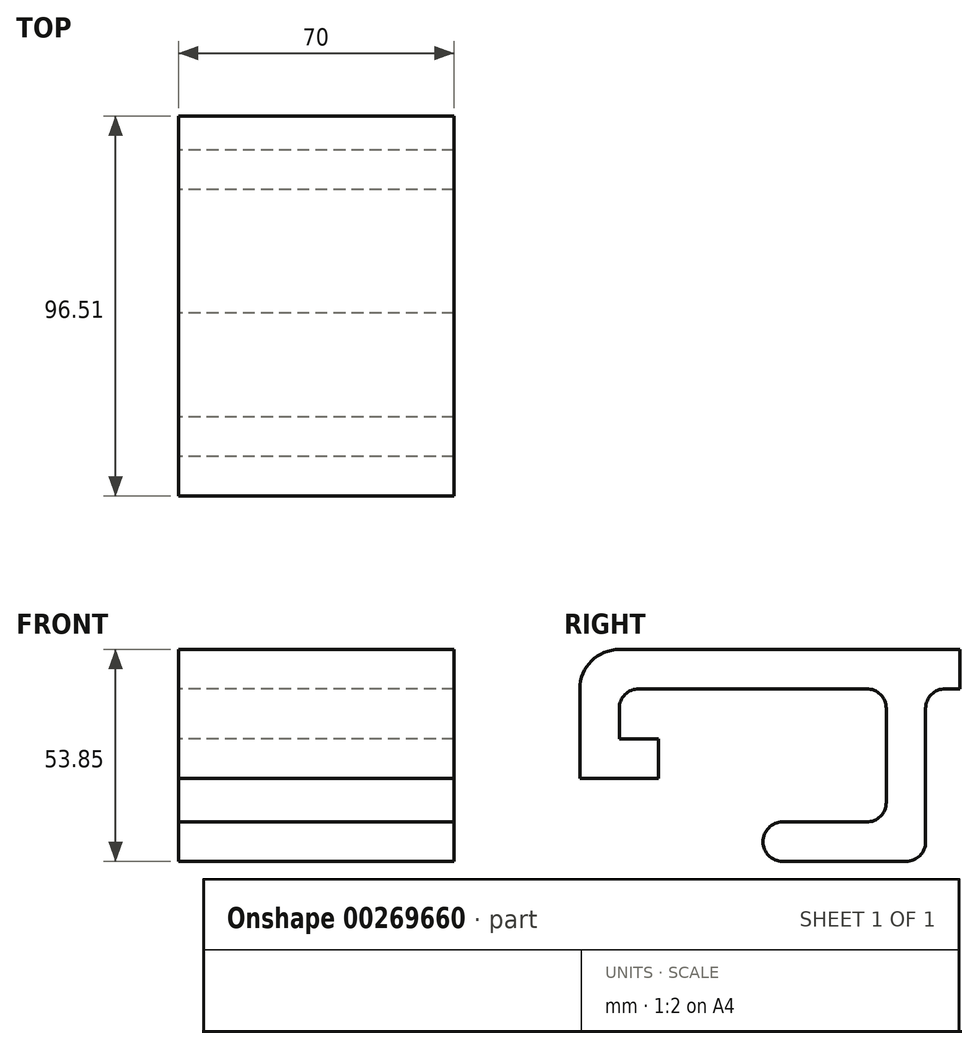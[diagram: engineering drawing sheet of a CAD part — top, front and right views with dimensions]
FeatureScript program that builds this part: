
annotation { "Feature Type Name" : "Feature", "Feature Type Description" : "" }
export const myFeature = defineFeature(function(context is Context, id is Id, definition is map)
    precondition{}
    {
        {
            var Q0;
            Q0=qCreatedBy(makeId("Right.planeOp"),FACE);
            var sketch = newSketch(context, id + "F0", { "sketchPlane" : qUnion([Q0])});
            skLineSegment(sketch, "E0", {"start": v(26.32, 0) * mm, "end": v(-31.51, 0) * mm});
            skLineSegment(sketch, "E1", {"start": v(-36.51, -5) * mm, "end": v(-36.51, -12.7) * mm});
            skLineSegment(sketch, "E2", {"start": v(-36.51, -12.7) * mm, "end": v(-26.51, -12.7) * mm});
            skLineSegment(sketch, "E3", {"start": v(-26.51, -12.7) * mm, "end": v(-26.51, -22.7) * mm});
            skLineSegment(sketch, "E4", {"start": v(-26.51, -22.7) * mm, "end": v(-46.51, -22.7) * mm});
            skLineSegment(sketch, "E5", {"start": v(-46.51, -22.7) * mm, "end": v(-46.51, 0) * mm});
            skLineSegment(sketch, "E6", {"start": v(-36.51, 10) * mm, "end": v(50, 10) * mm});
            skLineSegment(sketch, "E7", {"start": v(50, 10) * mm, "end": v(50, 0) * mm});
            skLineSegment(sketch, "E8", {"start": v(50, 0) * mm, "end": v(46.32, 0) * mm});
            skLineSegment(sketch, "E9", {"start": v(41.32, -5) * mm, "end": v(41.32, -38.85) * mm});
            skLineSegment(sketch, "E10", {"start": v(36.32, -43.85) * mm, "end": v(5, -43.85) * mm});
            skLineSegment(sketch, "E11", {"start": v(0, -38.85) * mm, "end": v(0, -38.85) * mm});
            skLineSegment(sketch, "E12", {"start": v(5, -33.85) * mm, "end": v(26.32, -33.85) * mm});
            skLineSegment(sketch, "E13", {"start": v(31.32, -28.85) * mm, "end": v(31.32, -5) * mm});
            skPoint(sketch, "E14.visualSharp", {"position": v(-36.51, 0) * mm});
            skArc(sketch, "E14.filletArc", {"start": v(-31.51, 0) * mm, "mid": v(-35.05, -1.46) * mm, "end": v(-36.51, -5) * mm});
            skPoint(sketch, "E15.visualSharp", {"position": v(-46.51, 10) * mm});
            skArc(sketch, "E15.filletArc", {"start": v(-36.51, 10) * mm, "mid": v(-43.58, 7.07) * mm, "end": v(-46.51, 0) * mm});
            skPoint(sketch, "E16.visualSharp", {"position": v(41.32, 0) * mm});
            skArc(sketch, "E16.filletArc", {"start": v(46.32, 0) * mm, "mid": v(42.79, -1.46) * mm, "end": v(41.32, -5) * mm});
            skPoint(sketch, "E17.visualSharp", {"position": v(31.32, 0) * mm});
            skArc(sketch, "E17.filletArc", {"start": v(31.32, -5) * mm, "mid": v(29.86, -1.46) * mm, "end": v(26.32, 0) * mm});
            skPoint(sketch, "E18.visualSharp", {"position": v(31.32, -33.85) * mm});
            skArc(sketch, "E18.filletArc", {"start": v(26.32, -33.85) * mm, "mid": v(29.86, -32.39) * mm, "end": v(31.32, -28.85) * mm});
            skPoint(sketch, "E19.visualSharp", {"position": v(41.32, -43.85) * mm});
            skArc(sketch, "E19.filletArc", {"start": v(36.32, -43.85) * mm, "mid": v(39.86, -42.39) * mm, "end": v(41.32, -38.85) * mm});
            skPoint(sketch, "E20.visualSharp", {"position": v(0, -33.85) * mm});
            skArc(sketch, "E20.filletArc", {"start": v(5, -33.85) * mm, "mid": v(1.46, -35.32) * mm, "end": v(0, -38.85) * mm});
            skPoint(sketch, "E21.visualSharp", {"position": v(0, -43.85) * mm});
            skArc(sketch, "E21.filletArc", {"start": v(0, -38.85) * mm, "mid": v(1.46, -42.39) * mm, "end": v(5, -43.85) * mm});
            skSolve(sketch);
        }
        {
            var Q0;
            Q0 = qSketchRegion(id + "F0", true);
            extrude(context, id + "F1", {"entities" : qUnion([Q0]), "endBound" : BoundingType.SYMMETRIC, "depth" : 70 * mm, "offsetDistance" : 25 * mm});
        }
    });
